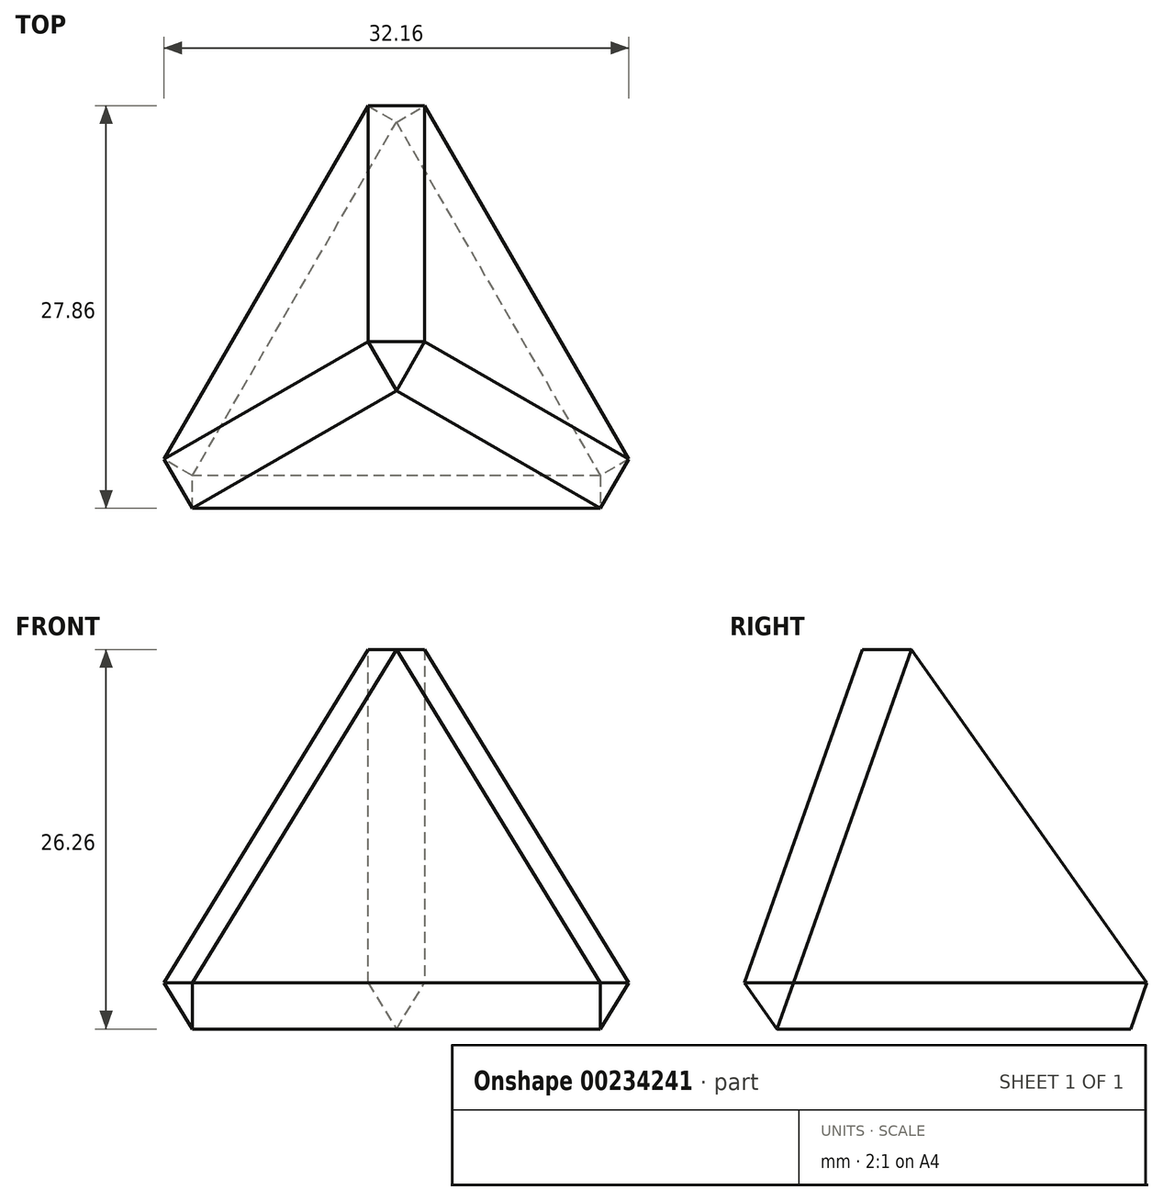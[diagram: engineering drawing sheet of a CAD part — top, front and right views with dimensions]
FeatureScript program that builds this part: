
annotation { "Feature Type Name" : "Feature", "Feature Type Description" : "" }
export const myFeature = defineFeature(function(context is Context, id is Id, definition is map)
    precondition{}
    {
        {
            var Q0;
            Q0=qCreatedBy(makeId("Top.planeOp"),FACE);
            var sketch = newSketch(context, id + "F0", { "sketchPlane" : qUnion([Q0])});
            skCircle(sketch, "E0.cCircle", {"center": v(0, 0) * mm, "radius": 11.55 * mm, "construction": true});
            skLineSegment(sketch, "E0.0", {"start": v(0, 23.1) * mm, "end": v(20, -11.55) * mm});
            skLineSegment(sketch, "E0.1", {"start": v(20, -11.55) * mm, "end": v(-20, -11.55) * mm});
            skLineSegment(sketch, "E0.2", {"start": v(-20, -11.55) * mm, "end": v(0, 23.1) * mm});
            skPoint(sketch, "E0.0.midPoint", {"position": v(10, 5.77) * mm});
            skLineSegment(sketch, "E1", {"start": v(0, 23.1) * mm, "end": v(0, 0) * mm, "construction": true});
            skLineSegment(sketch, "E2", {"start": v(0, 0) * mm, "end": v(-20, -11.55) * mm, "construction": true});
            skLineSegment(sketch, "E3", {"start": v(0, 0) * mm, "end": v(20, -11.55) * mm, "construction": true});
            skSolve(sketch);
        }
        {
            var Q0;
            Q0=qCreatedBy(makeId("Top.planeOp"),FACE);
            cPlane(context, id + "F1", {"entities" : qUnion([Q0]), "cplaneType" : CPlaneType.OFFSET, "offset" : 32.66 * mm, "width" : 150 * mm, "height" : 150 * mm});
        }
        {
            var Q0;
            Q0=qCreatedBy(id+"F1.planeOp",FACE);
            var sketch = newSketch(context, id + "F2", { "sketchPlane" : qUnion([Q0])});
            skPoint(sketch, "E4", {"position": v(0, 0) * mm});
            skSolve(sketch);
        }
        {
            var Q0;
            Q0=makeQuery(id+"F0.imprint","IMPRINT",FACE,{"disambiguationData":[TD([[makeQuery(id+"F0.imprint","IMPRINT",EDGE,{"derivedFrom":sQuery(id+"F0.wireOp",EDGE,"E0.0")}),-1.0]])]});
            var Q1;
            Q1=sQuery(id+"F2.wireOp",VERTEX,"E4");
            loft(context, id + "F3", {"sheetProfilesArray" : [{ "sheetProfileEntities" : qUnion([Q0]) }, { "sheetProfileEntities" : qUnion([Q1]) }]});
        }
        {
            var Q0;
            Q0=makeQuery(id+"F3.opLoft","SWEPT_EDGE",EDGE,{"disambiguationData":[OSD([sQuery(id+"F0.wireOp",EDGE,"E0.0"),sQuery(id+"F0.wireOp",EDGE,"E0.1"),sQuery(id+"F2.wireOp",VERTEX,"E4")])]});
            var Q1;
            Q1=makeQuery(id+"F3.opLoft","SWEPT_EDGE",EDGE,{"disambiguationData":[OSD([sQuery(id+"F0.wireOp",EDGE,"E0.1"),sQuery(id+"F0.wireOp",EDGE,"E0.2"),sQuery(id+"F2.wireOp",VERTEX,"E4")])]});
            var Q2;
            Q2=makeQuery(id+"F3.opLoft","SWEPT_EDGE",EDGE,{"disambiguationData":[OSD([sQuery(id+"F0.wireOp",EDGE,"E0.0"),sQuery(id+"F0.wireOp",EDGE,"E0.2"),sQuery(id+"F2.wireOp",VERTEX,"E4")])]});
            var Q3;
            {var subQ0=sQuery(id+"F0.wireOp",EDGE,"E0.1");var subQ1=sQuery(id+"F0.wireOp",EDGE,"E0.2");var subQ2=sQuery(id+"F0.wireOp",EDGE,"E0.0");Q3=makeQuery(id+"F3.opLoft","MID_CAP_EDGE",EDGE,{"disambiguationData":[OSD([subQ2,subQ0,subQ1]),TDD([makeQuery(id+"F0.imprint","INTERSECT",VERTEX,{"derivedFrom":[subQ2,subQ0]}),makeQuery(id+"F0.imprint","INTERSECT",VERTEX,{"derivedFrom":[subQ0,subQ1]}),makeQuery(id+"F0.imprint","IMPRINT",EDGE,{"derivedFrom":subQ0})])],"capPos":0.0});}
            var Q4;
            {var subQ0=sQuery(id+"F0.wireOp",EDGE,"E0.2");var subQ1=sQuery(id+"F0.wireOp",EDGE,"E0.1");var subQ2=sQuery(id+"F0.wireOp",EDGE,"E0.0");Q4=makeQuery(id+"F3.opLoft","MID_CAP_EDGE",EDGE,{"disambiguationData":[OSD([subQ2,subQ1,subQ0]),TDD([makeQuery(id+"F0.imprint","INTERSECT",VERTEX,{"derivedFrom":[subQ2,subQ0]}),makeQuery(id+"F0.imprint","INTERSECT",VERTEX,{"derivedFrom":[subQ1,subQ0]}),makeQuery(id+"F0.imprint","IMPRINT",EDGE,{"derivedFrom":subQ0})])],"capPos":0.0});}
            var Q5;
            {var subQ0=sQuery(id+"F0.wireOp",EDGE,"E0.0");var subQ1=sQuery(id+"F0.wireOp",EDGE,"E0.1");var subQ2=sQuery(id+"F0.wireOp",EDGE,"E0.2");Q5=makeQuery(id+"F3.opLoft","MID_CAP_EDGE",EDGE,{"disambiguationData":[OSD([subQ0,subQ1,subQ2]),TDD([makeQuery(id+"F0.imprint","INTERSECT",VERTEX,{"derivedFrom":[subQ0,subQ2]}),makeQuery(id+"F0.imprint","INTERSECT",VERTEX,{"derivedFrom":[subQ0,subQ1]}),makeQuery(id+"F0.imprint","IMPRINT",EDGE,{"derivedFrom":subQ0})])],"capPos":0.0});}
            chamfer(context, id + "F4", {"entities" : qUnion([Q0, Q1, Q2, Q3, Q4, Q5]), "width" : 2.4 * mm, "tangentPropagation" : true});
        }
    });
